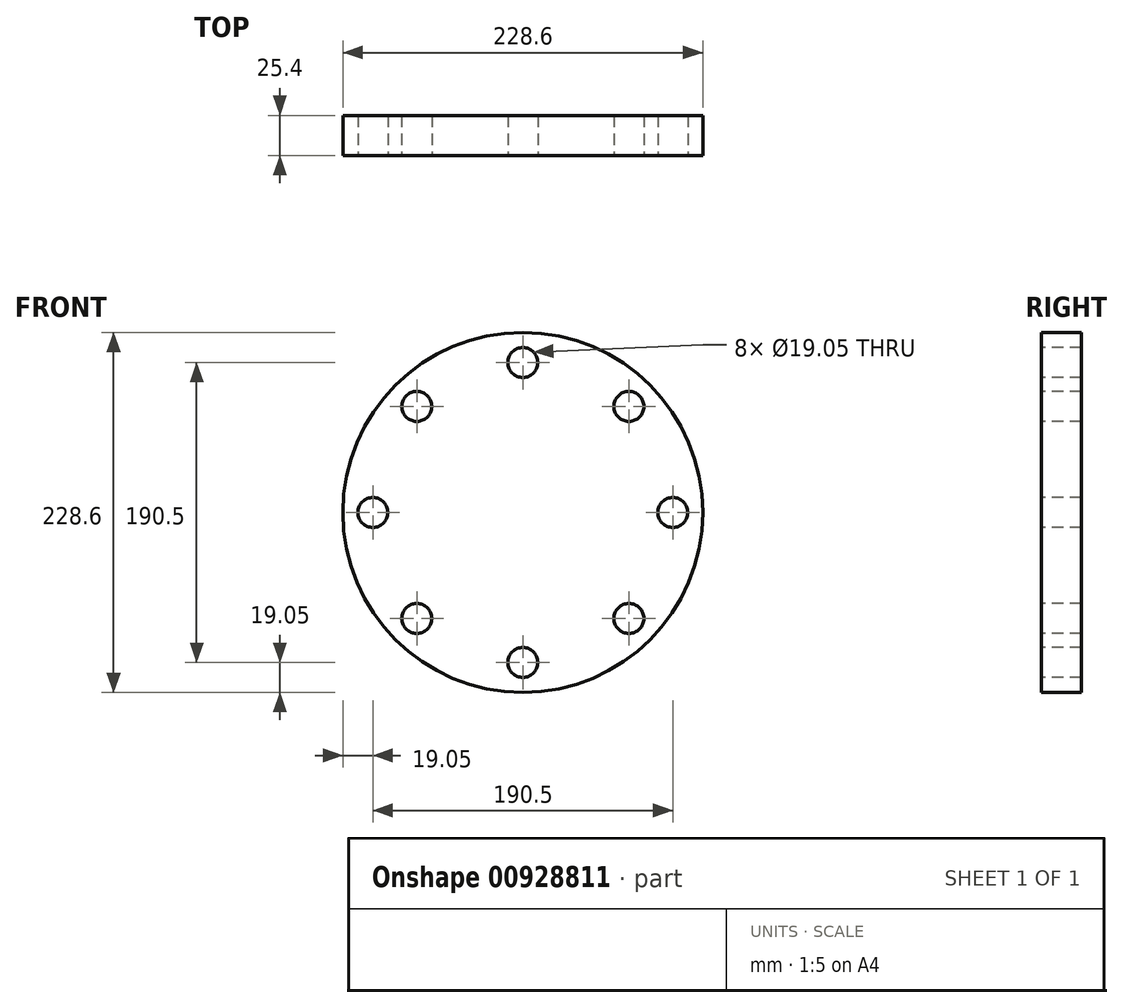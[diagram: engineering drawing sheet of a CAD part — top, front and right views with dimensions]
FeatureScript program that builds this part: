
annotation { "Feature Type Name" : "Feature", "Feature Type Description" : "" }
export const myFeature = defineFeature(function(context is Context, id is Id, definition is map)
    precondition{}
    {
        {
            var Q0;
            Q0=qCreatedBy(makeId("Top.planeOp"),FACE);
            var sketch = newSketch(context, id + "F0", { "sketchPlane" : qUnion([Q0])});
            skLineSegment(sketch, "E0", {"start": v(51.13, 0) * mm, "end": v(114.3, 0) * mm});
            skLineSegment(sketch, "E1", {"start": v(114.3, 0) * mm, "end": v(114.3, 25.4) * mm});
            skLineSegment(sketch, "E2", {"start": v(114.3, 25.4) * mm, "end": v(51.13, 25.4) * mm});
            skLineSegment(sketch, "E3", {"start": v(51.13, 25.4) * mm, "end": v(51.13, 0) * mm, "construction": true});
            skLineSegment(sketch, "E4", {"start": v(0, 25.4) * mm, "end": v(0, 0) * mm});
            skLineSegment(sketch, "E5", {"start": v(0, 0) * mm, "end": v(594.1, 0) * mm, "construction": true});
            skLineSegment(sketch, "E6.bottom", {"start": v(0, 0) * mm, "end": v(51.13, 0) * mm});
            skLineSegment(sketch, "E6.top", {"start": v(0, 25.4) * mm, "end": v(51.13, 25.4) * mm});
            skLineSegment(sketch, "E6.left", {"start": v(0, 0) * mm, "end": v(0, 25.4) * mm});
            skLineSegment(sketch, "E6.right", {"start": v(51.13, 0) * mm, "end": v(51.13, 25.4) * mm});
            skSolve(sketch);
        }
        {
            var Q0;
            Q0=qSketchRegion(id+"F0",true);
            var Q1;
            Q1=sQuery(id+"F0.wireOp",EDGE,"E4");
            revolve(context, id + "F1", {"surfaceOperationType" : NewSurfaceOperationType.NEW, "entities" : qUnion([Q0]), "axis" : qUnion([Q1]), "revolveType" : RevolveType.FULL});
        }
        {
            var Q0;
            Q0=makeQuery(id+"F1.opRevolve","SWEPT_FACE",FACE,{"disambiguationData":[OSD([sQuery(id+"F0.wireOp",EDGE,"E0")])]});
            var sketch = newSketch(context, id + "F2", { "sketchPlane" : qUnion([Q0])});
            skCircle(sketch, "E7", {"center": v(-95.25, 0) * mm, "radius": 9.53 * mm});
            skCircle(sketch, "E8.1.0", {"center": v(-67.35, -67.35) * mm, "radius": 9.53 * mm});
            skCircle(sketch, "E8.2.0", {"center": v(0, -95.25) * mm, "radius": 9.53 * mm});
            skCircle(sketch, "E8.3.0", {"center": v(67.35, -67.35) * mm, "radius": 9.53 * mm});
            skCircle(sketch, "E8.4.0", {"center": v(95.25, 0) * mm, "radius": 9.53 * mm});
            skCircle(sketch, "E8.5.0", {"center": v(67.35, 67.35) * mm, "radius": 9.53 * mm});
            skCircle(sketch, "E8.6.0", {"center": v(0, 95.25) * mm, "radius": 9.53 * mm});
            skCircle(sketch, "E8.7.0", {"center": v(-67.35, 67.35) * mm, "radius": 9.53 * mm});
            skPoint(sketch, "E8.center", {"position": v(0, 0) * mm});
            skSolve(sketch);
        }
        {
            var Q0;
            Q0=qSketchRegion(id+"F2",true);
            var Q1;
            Q1=makeQuery(id+"F1.opRevolve","SWEPT_FACE",FACE,{"disambiguationData":[OSD([sQuery(id+"F0.wireOp",EDGE,"E2")])]});
            var Q2;
            Q2=makeQuery(id+"F1.opRevolve","SWEPT_FACE",FACE,{"disambiguationData":[OSD([sQuery(id+"F0.wireOp",EDGE,"288f55ee-0791-4258-b4ab-a728cb0339146.MirrorCS")])]});
            extrude(context, id + "F3", {"entities" : qUnion([Q0]), "operationType" : NewBodyOperationType.REMOVE, "endBound" : BoundingType.UP_TO_SURFACE, "oppositeDirection" : true, "depth" : 25.4 * mm, "endBoundEntityFace" : qUnion([Q1]), "offsetDistance" : 25.4 * mm});
        }
    });
